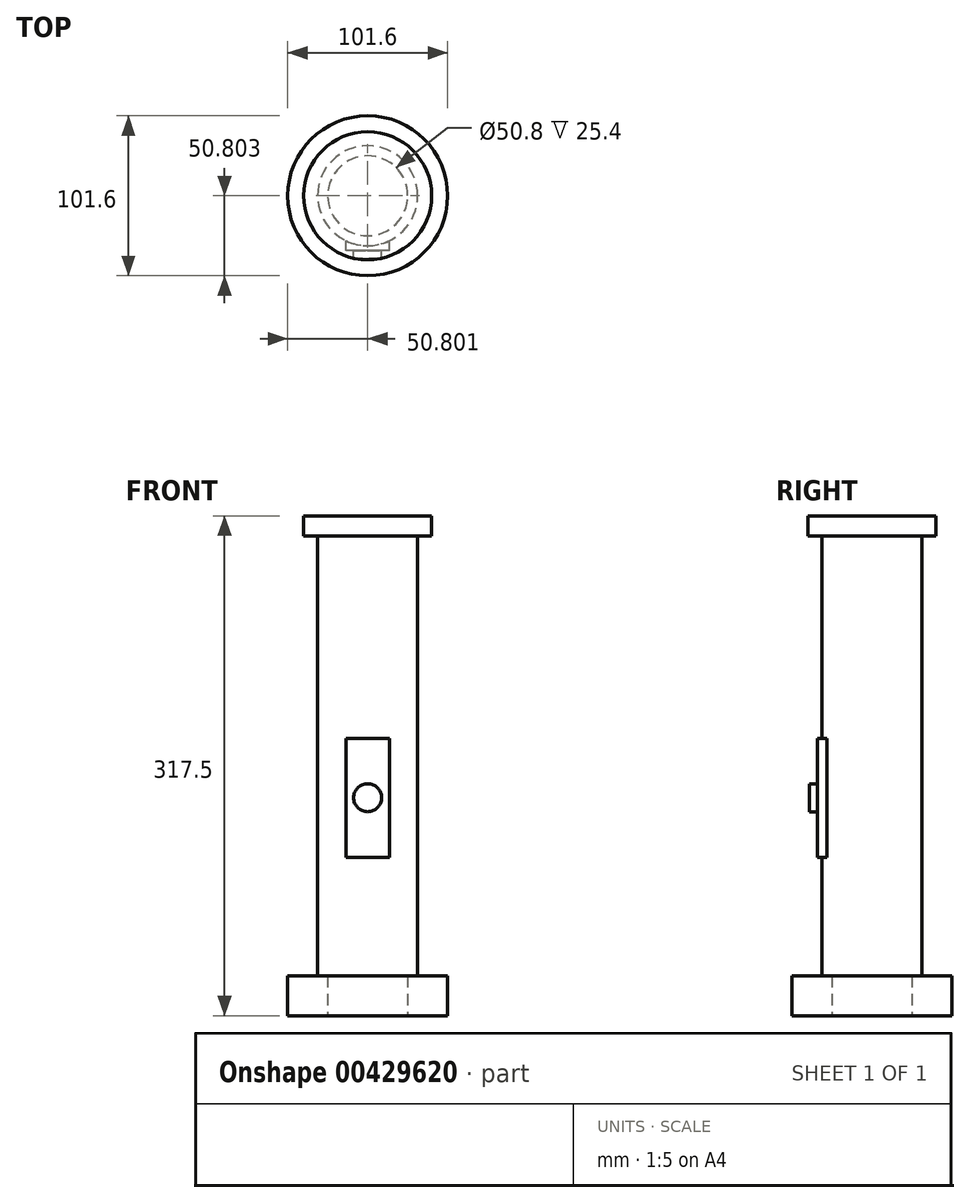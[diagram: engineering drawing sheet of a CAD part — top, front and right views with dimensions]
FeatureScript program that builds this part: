
annotation { "Feature Type Name" : "Feature", "Feature Type Description" : "" }
export const myFeature = defineFeature(function(context is Context, id is Id, definition is map)
    precondition{}
    {
        {
            var Q0;
            Q0=qCreatedBy(makeId("Top.planeOp"),FACE);
            var sketch = newSketch(context, id + "F0", { "sketchPlane" : qUnion([Q0])});
            skCircle(sketch, "E0", {"center": v(-63.05, 27.1) * mm, "radius": 50.8 * mm});
            skSolve(sketch);
        }
        {
            var Q0;
            Q0=makeQuery(id+"F0.imprint","IMPRINT",FACE,{"disambiguationData":[TD([[makeQuery(id+"F0.imprint","IMPRINT",EDGE,{"derivedFrom":sQuery(id+"F0.wireOp",EDGE,"E0")}),1.0]])]});
            var sketch = newSketch(context, id + "F1", { "sketchPlane" : qUnion([Q0])});
            skCircle(sketch, "E1", {"center": v(-63.06, 27.1) * mm, "radius": 31.75 * mm});
            skSolve(sketch);
        }
        {
            var Q0;
            Q0 = qSketchRegion(id + "F1", true);
            extrude(context, id + "F2", {"entities" : qUnion([Q0]), "oppositeDirection" : true, "depth" : 279.4 * mm});
        }
        {
            var Q0;
            Q0=makeQuery(id+"F2.opExtrude","CAP_FACE",FACE,{"disambiguationData":[OSD([sQuery(id+"F1.wireOp",EDGE,"E1")])],"isStart":false});
            var sketch = newSketch(context, id + "F3", { "sketchPlane" : qUnion([Q0])});
            skCircle(sketch, "E2", {"center": v(-63.06, -27.1) * mm, "radius": 50.8 * mm});
            skSolve(sketch);
        }
        {
            var Q0;
            Q0 = qSketchRegion(id + "F3", true);
            extrude(context, id + "F4", {"entities" : qUnion([Q0]), "operationType" : NewBodyOperationType.ADD, "depth" : 50.8 * mm});
        }
        {
            var Q0;
            Q0=makeQuery(id+"F2.opExtrude","CAP_FACE",FACE,{"disambiguationData":[OSD([sQuery(id+"F1.wireOp",EDGE,"E1")])],"isStart":true});
            var sketch = newSketch(context, id + "F5", { "sketchPlane" : qUnion([Q0])});
            skCircle(sketch, "E3", {"center": v(-63.06, 27.1) * mm, "radius": 40.64 * mm});
            skSolve(sketch);
        }
        {
            var Q0;
            Q0 = qSketchRegion(id + "F5", true);
            extrude(context, id + "F6", {"entities" : qUnion([Q0]), "operationType" : NewBodyOperationType.ADD, "depth" : 12.7 * mm});
        }
        {
            var Q0;
            Q0=makeQuery(id+"F4.opExtrude","CAP_FACE",FACE,{"disambiguationData":[OSD([sQuery(id+"F3.wireOp",EDGE,"E2")])],"isStart":false});
            extrude(context, id + "F7", {"entities" : qUnion([Q0]), "operationType" : NewBodyOperationType.REMOVE, "oppositeDirection" : true, "depth" : 25.4 * mm});
        }
        {
            var Q0;
            Q0=qCreatedBy(makeId("Front.planeOp"),FACE);
            var sketch = newSketch(context, id + "F8", { "sketchPlane" : qUnion([Q0])});
            skLineSegment(sketch, "E4.bottom", {"start": v(-49.25, -204.17) * mm, "end": v(-76.9, -204.17) * mm});
            skLineSegment(sketch, "E4.top", {"start": v(-49.25, -128.59) * mm, "end": v(-76.9, -128.59) * mm});
            skLineSegment(sketch, "E4.left", {"start": v(-49.25, -204.17) * mm, "end": v(-49.25, -128.59) * mm});
            skLineSegment(sketch, "E4.right", {"start": v(-76.9, -204.17) * mm, "end": v(-76.9, -128.59) * mm});
            skPoint(sketch, "E4.middle", {"position": v(-63.07, -166.38) * mm});
            skSolve(sketch);
        }
        {
            var Q0;
            Q0 = qSketchRegion(id + "F8", true);
            extrude(context, id + "F9", {"entities" : qUnion([Q0]), "operationType" : NewBodyOperationType.ADD, "depth" : 7.62 * mm});
        }
        {
            var Q0;
            Q0=makeQuery(id+"F7.boolean.opBoolean","COPY",FACE,{"derivedFrom":makeQuery(id+"F7.opExtrude","CAP_FACE",FACE,{"disambiguationData":[OSD([sQuery(id+"F3.wireOp",EDGE,"E2")])],"isStart":false})});
            var sketch = newSketch(context, id + "F10", { "sketchPlane" : qUnion([Q0])});
            skCircle(sketch, "E5", {"center": v(-63.06, -27.1) * mm, "radius": 25.4 * mm});
            skSolve(sketch);
        }
        {
            var Q0;
            Q0 = qSketchRegion(id + "F10", true);
            extrude(context, id + "F11", {"entities" : qUnion([Q0]), "operationType" : NewBodyOperationType.REMOVE, "oppositeDirection" : true, "depth" : 25.4 * mm});
        }
        {
            var Q0;
            Q0=makeQuery(id+"F9.opExtrude","CAP_FACE",FACE,{"disambiguationData":[OSD([sQuery(id+"F8.wireOp",EDGE,"E4.bottom"),sQuery(id+"F8.wireOp",EDGE,"E4.top"),sQuery(id+"F8.wireOp",EDGE,"E4.left"),sQuery(id+"F8.wireOp",EDGE,"E4.right")])],"isStart":false});
            var sketch = newSketch(context, id + "F12", { "sketchPlane" : qUnion([Q0])});
            skCircle(sketch, "E6", {"center": v(-63.07, -166.38) * mm, "radius": 8.9 * mm});
            skPoint(sketch, "E6.centerSnap0", {"position": v(-63.07, -128.59) * mm});
            skPoint(sketch, "E6.centerSnap1", {"position": v(-49.25, -166.38) * mm});
            skSolve(sketch);
        }
        {
            var Q0;
            Q0 = qSketchRegion(id + "F12", true);
            extrude(context, id + "F13", {"entities" : qUnion([Q0]), "operationType" : NewBodyOperationType.ADD, "depth" : 5.08 * mm});
        }
    });
